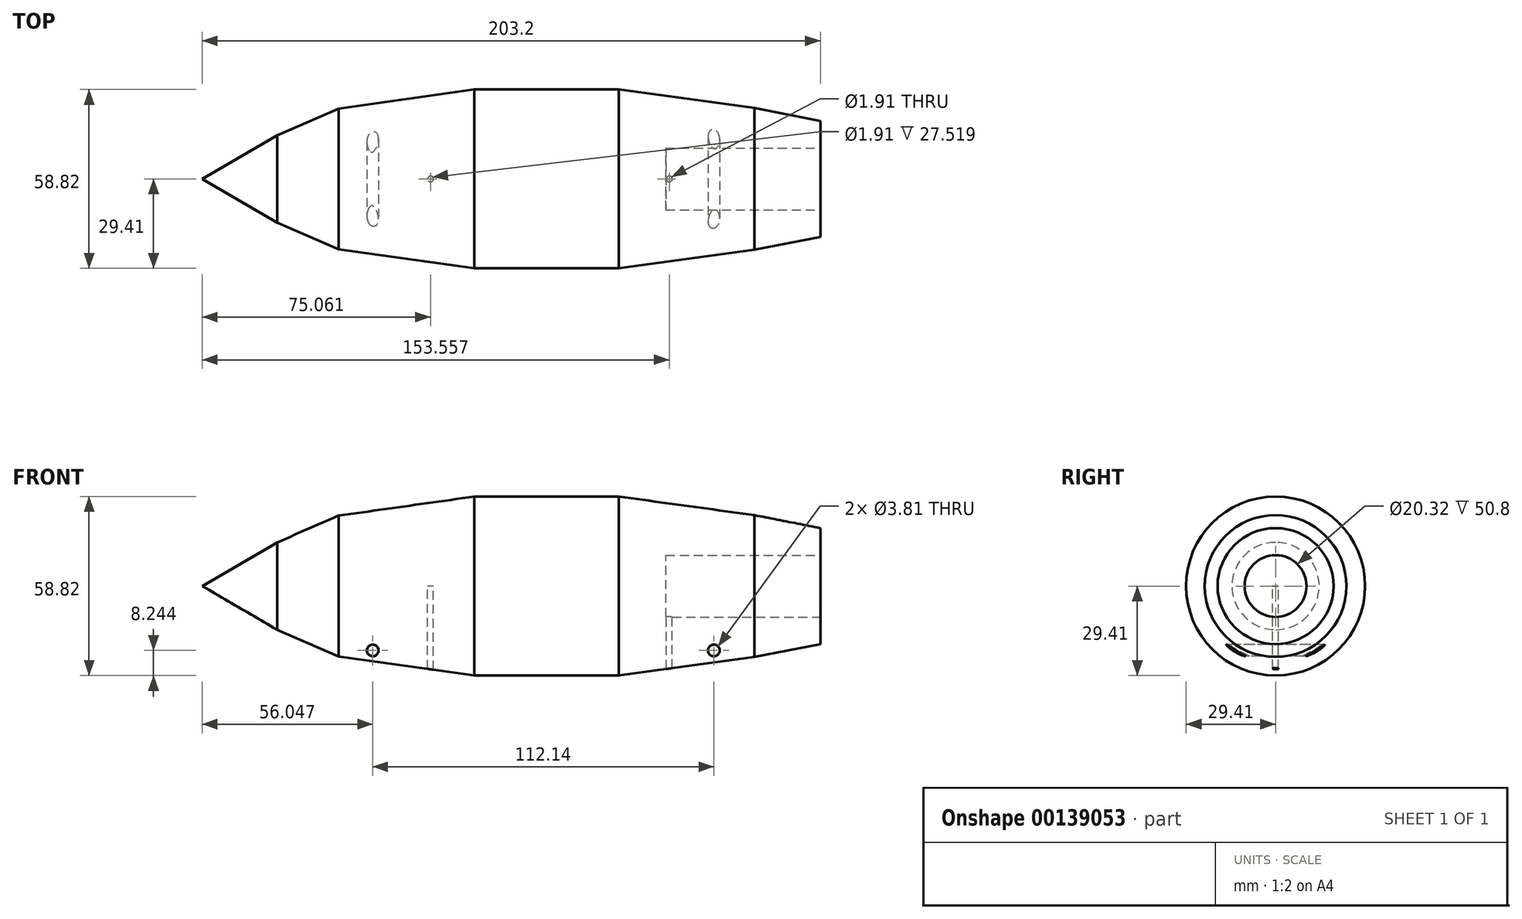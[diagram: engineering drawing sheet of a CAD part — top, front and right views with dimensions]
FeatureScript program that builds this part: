
annotation { "Feature Type Name" : "Feature", "Feature Type Description" : "" }
export const myFeature = defineFeature(function(context is Context, id is Id, definition is map)
    precondition{}
    {
        {
            var Q0;
            Q0=qCreatedBy(makeId("Front.planeOp"),FACE);
            var sketch = newSketch(context, id + "F0", { "sketchPlane" : qUnion([Q0])});
            skLineSegment(sketch, "E0", {"start": v(-101.4, 0) * mm, "end": v(101.8, 0) * mm});
            skLineSegment(sketch, "E1", {"start": v(101.8, 0) * mm, "end": v(101.8, 19.05) * mm});
            skLineSegment(sketch, "E2", {"start": v(101.8, 19.05) * mm, "end": v(80.13, 23.3) * mm});
            skLineSegment(sketch, "E3", {"start": v(80.13, 23.3) * mm, "end": v(35.6, 29.4) * mm});
            skLineSegment(sketch, "E4", {"start": v(35.6, 29.4) * mm, "end": v(-11.97, 29.4) * mm});
            skLineSegment(sketch, "E5", {"start": v(-11.97, 29.4) * mm, "end": v(-56.47, 23.14) * mm});
            skLineSegment(sketch, "E6", {"start": v(-56.47, 23.14) * mm, "end": v(-76.73, 14.35) * mm});
            skLineSegment(sketch, "E7", {"start": v(-76.73, 14.35) * mm, "end": v(-101.4, 0) * mm});
            skSolve(sketch);
        }
        {
            var Q0;
            Q0=makeQuery(id+"F0.imprint","IMPRINT",FACE,{"disambiguationData":[TD([[makeQuery(id+"F0.imprint","IMPRINT",EDGE,{"derivedFrom":sQuery(id+"F0.wireOp",EDGE,"E0")}),1.0]])]});
            var Q1;
            Q1=sQuery(id+"F0.wireOp",EDGE,"E0");
            revolve(context, id + "F1", {"entities" : qUnion([Q0]), "axis" : qUnion([Q1]), "revolveType" : RevolveType.FULL});
        }
        {
            var Q0;
            Q0=qCreatedBy(makeId("Front.planeOp"),FACE);
            var sketch = newSketch(context, id + "F2", { "sketchPlane" : qUnion([Q0])});
            skCircle(sketch, "E8", {"center": v(-45.34, -21.17) * mm, "radius": 1.9 * mm});
            skCircle(sketch, "E9", {"center": v(66.8, -21.17) * mm, "radius": 1.9 * mm});
            skSolve(sketch);
        }
        {
            var Q0;
            Q0 = qSketchRegion(id + "F2", true);
            extrude(context, id + "F3", {"entities" : qUnion([Q0]), "operationType" : NewBodyOperationType.REMOVE, "endBound" : BoundingType.THROUGH_ALL, "oppositeDirection" : true, "depth" : 25.4 * mm, "hasSecondDirection" : true, "secondDirectionBound" : SecondDirectionBoundingType.THROUGH_ALL, "secondDirectionOppositeDirection" : false, "secondDirectionDepth" : 12.7 * mm});
        }
        {
            var Q0;
            Q0=makeQuery(id+"F1.opRevolve","SWEPT_FACE",FACE,{"disambiguationData":[OSD([sQuery(id+"F0.wireOp",EDGE,"E1")])]});
            var sketch = newSketch(context, id + "F4", { "sketchPlane" : qUnion([Q0])});
            skCircle(sketch, "E10", {"center": v(0, 0) * mm, "radius": 10.16 * mm});
            skSolve(sketch);
        }
        {
            var Q0;
            Q0=makeQuery(id+"F4.imprint","IMPRINT",FACE,{"disambiguationData":[TD([[makeQuery(id+"F4.imprint","IMPRINT",EDGE,{"derivedFrom":sQuery(id+"F4.wireOp",EDGE,"E10")}),1.0]])]});
            extrude(context, id + "F5", {"entities" : qUnion([Q0]), "operationType" : NewBodyOperationType.REMOVE, "oppositeDirection" : true, "depth" : 50.8 * mm});
        }
        {
            var Q0;
            Q0=qCreatedBy(makeId("Top.planeOp"),FACE);
            var sketch = newSketch(context, id + "F6", { "sketchPlane" : qUnion([Q0])});
            skCircle(sketch, "E11", {"center": v(-26.33, 0) * mm, "radius": 0.95 * mm});
            skCircle(sketch, "E12", {"center": v(52.17, 0) * mm, "radius": 0.95 * mm});
            skSolve(sketch);
        }
        {
            var Q0;
            Q0 = qSketchRegion(id + "F6", true);
            extrude(context, id + "F7", {"entities" : qUnion([Q0]), "operationType" : NewBodyOperationType.REMOVE, "oppositeDirection" : true, "depth" : 38.1 * mm});
        }
    });
